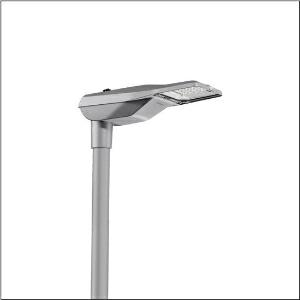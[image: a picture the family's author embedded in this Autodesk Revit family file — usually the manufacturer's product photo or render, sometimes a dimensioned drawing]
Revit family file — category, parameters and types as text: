
# Revit family: streetlight_sl_21_micro___st1_0a_5xe1d43s08db_64f0
name_source: partatom
category: Lighting Fixtures
units: mm (PartAtom-declared; Revit-internal decimal feet)

## family parameters
Cut with Voids When Loaded = No
Host = Face
Light Source = No
Part Type = Normal
Room Calculation Point = No
Round Connector Dimension = Use Diameter
Shared = No

## types (1)
- --- (1 x LED, 5320 lm, 39.1 W, 4000K)
    Apparent Load = 39 VA
    CIE Flux Codes = 37 72 97 100 100
    Color Rendering = 70
    Color Temperature = 4000K
    Default Elevation = 1800 mm
    Description = Streetlight SL 21 micro, mast luminaire, primary light control with lens, of PMMA, primary optical cover: cover, of toughened safety glass, transparent, light distribution: ST1.0a, light emission: direct distribution, primary light characteristic: asymmetric, installation type: side-entry, post-top, LED, High Power LED, rated luminous flux: 5.320lm, luminous efficacy: 136lm/W, light colour: 740, colour temperature: 4000K, control: flexible luminous flux parameterisation, time-dependent luminous flux control, constant luminous flux control, overheat protection, presetting dimming logarithmic, mains connection: 220..240V, AC, 50/60Hz, start of lifetime: 39W, end of service life: 41W, reduction: 18W, luminaire housing, of diecast aluminium, powder-coated, Siteco® metallic grey (DB 702S), corrosivity category C5 mid according to DIN EN ISO 12944, please order mast flange separately, inclination adjustable: 0°, 5°, 10°, 15°, sealing non-destructively replaceable, multi-level sealing system, length: 528mm, width: 235mm, height: 110mm, mast flange for spigot size: 42mm (side-entry): 5XC10008XM4, 60/48mm (side-entry/post-top): 5XC10108XM2, 76/60mm (side-entry/post-top): 5XC10108XM1, Smart Interface above, protection rating (complete): IP66, insulation class (complete): insulation class II (safety insulation), certification: CE, ENEC, ENEC+, VDE, impact resistance: IK09, permissible operating ambient temperature for outdoor applications: -40..+50°C, standard-compliant lighting for roads and squares, packaging unit: 1 piece

Light Distribution: ST1.0a
    Height = 110 mm
    Lamp = 1 x LED
    Lamp Light Flux = 5320 lm
    Lamp Power = 39.1 W
    Lamp count = 1
    Length = 528 mm
    Luminous efficacy = 136 lm/W
    Manufacturer = Siteco
    ModVariant = No
    Model = 5XE1D43S08DB
    Number of Poles = 1
    OnlyDefault = Yes
    Power Factor = 1
    Product Name = Streetlight SL 21 micro | ST1.0a
    Product group = mast luminaire | pylon top
    ProductGroupID = 6100
    Protection Class = Protection class II
    Protection Degree = IP 66
    RLX_Detail_Level = 1
    RLX_Emergency_Light_Flux = 0 lm
    RLX_Emergency_Type = 0
    RLX_Emergency_Type_DB = No
    RlxData = <blob elided: 98237 chars, md5=246e6f13>
    Socket = socket
    Standby Power = 0 W
    System Light Flux = 5320 lm
    System Power = 39 W
    Type Comments = factory setting: luminous flux: 100 % | dim-lin: 254 | 765 mA
    Type Image = l_1277292.jpg
    URL = http://relux.com
    VarID = @adj_088101
    Voltage = 0 V
    Weight = 0.00 kg
    Width = 235 mm

## geometry (parser evidence)
native form markers: Blend x4, Sweep x11
no freeform markers — native parametric forms only
